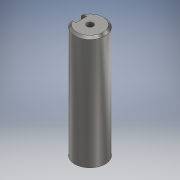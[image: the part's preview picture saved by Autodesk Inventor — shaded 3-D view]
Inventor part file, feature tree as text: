
AUTODESK INVENTOR PART (.ipt)
format: ipt  version: 2018 (Build 220112000, 112)  size: 122,880 bytes
history: native  units: mm
features: extrude x2, sketch x2, hole x1, plane x1, chamfer x1, projected_geometry x1
ambient origin geometry x8: Origin, YZ Plane, XZ Plane, XY Plane, X Axis, Y Axis, Z Axis, Center Point
bodies: Solid1 (feature_tree)
feature tree (8):
  extrude  "Extrusion1"  Depth=52.0mm TaperAngle=0.0deg
  hole  "Hole1"  [1 undecoded]
  plane  "Work Plane1"
  extrude  "Extrusion2"  TaperAngle=0.0deg  [1 undecoded]
  chamfer  "Chamfer1"  Distance=3.0mm
  sketch  "Sketch1"  dims[d0=14.0mm d1=52.0mm d2=0.0mm]
  sketch  "Sketch2"  dims[d3=10.0mm d4=10.0mm d5=3.0mm d6=6.0mm d7=4.0mm d8=2.0mm d9=90.0deg d10=13.0mm d11=0.0mm d12=5.0mm d14=0.0mm d17=3.0mm d18=0.0mm d19=1.0mm d20=2.0mm d21=45.0deg]
  projected_geometry  "Projected Loop1"
note: 2 required parameter values undecoded (feature->parameter linkage not recoverable at this tier; creation-order binding heuristic only, values carry confidence <= 0.55)
